# Revit family: Шкафы климатические навесные (без крыши)
name_source: partatom
category: Обобщенные модели
units: mm (PartAtom-declared; Revit-internal decimal feet)

## family parameters
Всегда вертикально = Да
Может служить основой для арматурных стержней = Нет
На основе рабочей плоскости = Нет
Общий = Нет
При загрузке вырезать с полостями = Нет
Размер круглого соединителя = Использовать диаметр
Тип детали = Нормальный
Точка расчета площади = Нет

## types (20) — shared parameters
ADSK_URL документации изделия = sert_shkt.PDF (ssd.ru)
ADSK_Единица измерения = шт
ADSK_Завод-изготовитель = АО СВЯЗЬСТРОЙДЕТАЛЬ
ADSK_Размер_Ширина = 678 мм
Материал Каркаса = RAL 7035
Материал букв = Металл красный
Материал ручек = Металл черный
Толщина -4 = -4 мм
Толщина 25 = 25 мм
Толщина 4 = 4 мм
Толщина 5 = 5 мм
zero-valued in all types: Ноль

## per-type parameters (varying)
| type | 3й-ряд | ADSK_URL страницы изделия | ADSK_Код изделия | ADSK_Масса_Текст | ADSK_Наименование | ADSK_Размер_Высота | ADSK_Размер_Глубина | Описание | Ручка центр | Ручки не центр |
| ШКТ-НВ-6U (700х350мм) | Нет | Шкаф климатический телекоммуникационный навесной 19. 6U(600x350)  ШКТ-НВ-6U-600-350 ССД ( 130411-00801 ) (ssd.ru) | 130411-00801 | 17 | Шкаф климатический телекоммуникационный навесной 19&quot. 6U(600x350)  ШКТ-НВ-6U-600-350 ССД | 290 мм | 350 мм | Шкаф климатический телекоммуникационный навесной 19&quot. 6U(600x350)  ШКТ-НВ-6U-600-350 ССД | Да | Нет |
| ШКТ-НВ-6U (700х450мм) | Нет | Шкаф климатический телекоммуникационный навесной 19.  6U(600x450)  ШКТ-НВ-6U-600-450 ССД ( 130411-00802 ) (ssd.ru) | 130411-00802 | 19 | Шкаф климатический телекоммуникационный навесной 19&quot.  6U(600x450)  ШКТ-НВ-6U-600-450 ССД | 290 мм | 450 мм | Шкаф климатический телекоммуникационный навесной 19&quot.  6U(600x450)  ШКТ-НВ-6U-600-450 ССД | Да | Нет |
| ШКТ-НВ-6U (700х550мм) | Нет | Шкаф климатический телекоммуникационный навесной 19.  6U(600x550)  ШКТ-НВ-6U-600-550 ССД ( 130411-00803 ) (ssd.ru) | 130411-00803 | 21 | Шкаф климатический телекоммуникационный навесной 19&quot.  6U(600x550)  ШКТ-НВ-6U-600-550 ССД | 290 мм | 550 мм | Шкаф климатический телекоммуникационный навесной 19&quot.  6U(600x450)  ШКТ-НВ-6U-600-450 ССД | Да | Нет |
| ШКТ-НВ-6U (700х650мм) | Нет | Шкаф климатический телекоммуникационный навесной 19. 6U(600x650)  ШКТ-НВ-6U-600-650 ССД ( 130411-00804 ) (ssd.ru) | 130411-00804 | 23 | Шкаф климатический телекоммуникационный навесной 19&quot. 6U(600x650)  ШКТ-НВ-6U-600-650 ССД | 290 мм | 650 мм | Шкаф климатический телекоммуникационный навесной 19&quot. 6U(600x650)  ШКТ-НВ-6U-600-650 ССД | Да | Нет |
| ШКТ-НВ-9U (700х350мм) | Нет | Шкаф климатический телекоммуникационный навесной 19.  9U(600x350)  ШКТ-НВ-9U-600-350 ССД ( 130411-00805 ) (ssd.ru) | 130411-00805 | 25 | Шкаф климатический телекоммуникационный навесной 19&quot.  9U(600x350)  ШКТ-НВ-9U-600-350 ССД | 440 мм | 350 мм | Шкаф климатический телекоммуникационный навесной 19&quot.  9U(600x350)  ШКТ-НВ-9U-600-350 ССД | Нет | Да |
| ШКТ-НВ-9U (700х450мм) | Нет | Шкаф климатический телекоммуникационный навесной 19. 9U(600x450)  ШКТ-НВ-9U-600-450 ССД ( 130411-00806 ) (ssd.ru) | 130411-00806 | 28 | Шкаф климатический телекоммуникационный навесной 19&quot. 9U(700x450)  ШКТ-НВ-9U-600-450 ССД | 440 мм | 450 мм | Шкаф климатический телекоммуникационный навесной 19&quot. 9U(700x450)  ШКТ-НВ-9U-600-450 ССД | Нет | Да |
| ШКТ-НВ-9U (700х550мм) | Нет | Шкаф климатический телекоммуникационный навесной 19.  9U(600x550)  ШКТ-НВ-9U-600-550 ССД ( 130411-00807 ) (ssd.ru) | 130411-00807 | 31 | Шкаф климатический телекоммуникационный навесной 19&quot.  9U(600x550)  ШКТ-НВ-9U-600-550 ССД | 440 мм | 550 мм | Шкаф климатический телекоммуникационный навесной 19&quot.  9U(600x550)  ШКТ-НВ-9U-600-550 ССД | Нет | Да |
| ШКТ-НВ-9U (700х650мм) | Нет | Шкаф климатический телекоммуникационный навесной 19. 9U(600x650)  ШКТ-НВ-9U-600-650 ССД ( 130411-00808 ) (ssd.ru) | 130411-00808 | 34 | Шкаф климатический телекоммуникационный навесной 19&quot. 9U(600x650)  ШКТ-НВ-9U-600-650 ССД | 440 мм | 650 мм | Шкаф климатический телекоммуникационный навесной 19&quot. 9U(600x650)  ШКТ-НВ-9U-600-650 ССД | Нет | Да |
| ШКТ-НВ-12U (600х350мм) | Нет | Шкаф климатический телекоммуникационный навесной 19. 12U(600x350)  ШКТ-НВ-12U-600-350 ССД ( 130411-00809 ) (ssd.ru) | 130411-00809 | 36 | Шкаф климатический телекоммуникационный навесной 19&quot. 12U(600x350)  ШКТ-НВ-12U-600-350 ССД | 580 мм | 350 мм | Шкаф климатический телекоммуникационный навесной 19&quot. 12U(600x350)  ШКТ-НВ-12U-600-350 ССД | Нет | Да |
| ШКТ-НВ-12U (600х450мм) | Нет | Шкаф климатический телекоммуникационный навесной 19. 12U(600x450)  ШКТ-НВ-12U-600-450 ССД ( 130411-00810 ) (ssd.ru) | 130411-00810 | 40 | Шкаф климатический телекоммуникационный навесной 19&quot. 12U(600x450)  ШКТ-НВ-12U-600-450 ССД | 580 мм | 450 мм | Шкаф климатический телекоммуникационный навесной 19&quot. 12U(600x450)  ШКТ-НВ-12U-600-450 ССД | Нет | Да |
| ШКТ-НВ-12U (600х550мм) | Нет | Шкаф телекоммуникационный климатический навесной 19. 12U(600x550)  ШКТ-НВ-12U-600-550 ССД ( 130411-00811 ) (ssd.ru) | 130411-00811 | 43 | Шкаф телекоммуникационный климатический навесной 19&quot. 12U(600x550)  ШКТ-НВ-12U-600-550 ССД | 580 мм | 550 мм | Шкаф телекоммуникационный климатический навесной 19&quot. 12U(600x550)  ШКТ-НВ-12U-600-550 ССД | Нет | Да |
| ШКТ-НВ-12U (600х650мм) | Нет | Шкаф климатический телекоммуникационный навесной 19. 12U(600x650)  ШКТ-НВ-12U-600-650 ССД ( 130411-00812 ) (ssd.ru) | 130411-00812 | 47 | Шкаф климатический телекоммуникационный навесной 19&quot. 12U(600x650)  ШКТ-НВ-12U-600-650 ССД | 580 мм | 650 мм | Шкаф климатический телекоммуникационный навесной 19&quot. 12U(600x650)  ШКТ-НВ-12U-600-650 ССД | Нет | Да |
| ШКТ-НВ-15U (600х350мм) | Да | Шкаф климатический телекоммуникационный навесной 19. 15U(600x350)  ШКТ-НВ-15U-600-350 ССД ( 130411-00813 ) (ssd.ru) | 130411-00813 | 42 | Шкаф климатический телекоммуникационный навесной 19&quot. 15U(600x350)  ШКТ-НВ-15U-600-350 ССД | 714 мм | 350 мм | Шкаф климатический телекоммуникационный навесной 19&quot. 15U(600x350)  ШКТ-НВ-15U-600-350 ССД | Нет | Да |
| ШКТ-НВ-15U (600х450мм) | Да | Шкаф климатический телекоммуникационный навесной 19. 15U(600x450)  ШКТ-НВ-15U-600-450 ССД ( 130411-00814 ) (ssd.ru) | 130411-00814 | 46 | Шкаф климатический телекоммуникационный навесной 19&quot. 15U(600x450)  ШКТ-НВ-15U-600-450 ССД | 714 мм | 450 мм | Шкаф климатический телекоммуникационный навесной 19&quot. 15U(600x450)  ШКТ-НВ-15U-600-450 ССД | Нет | Да |
| ШКТ-НВ-15U (600х550мм) | Да | Шкаф климатический телекоммуникационный навесной 19. 15U(600x550)  ШКТ-НВ-15U-600-550 ССД ( 130411-00815 ) (ssd.ru) | 130411-00815 | 50 | Шкаф климатический телекоммуникационный навесной 19&quot. 15U(600x550)  ШКТ-НВ-15U-600-550 ССД | 714 мм | 550 мм | Шкаф климатический телекоммуникационный навесной 19&quot. 15U(600x550)  ШКТ-НВ-15U-600-550 ССД | Нет | Да |
| ШКТ-НВ-15U (600х650мм) | Да | Шкаф климатический телекоммуникационный навесной 19. 15U(600x650)  ШКТ-НВ-15U-600-650 ССД ( 130411-00816 ) (ssd.ru) | 130411-00816 | 54 | Шкаф климатический телекоммуникационный навесной 19&quot. 15U(600x650)  ШКТ-НВ-15U-600-650 ССД | 714 мм | 650 мм | Шкаф климатический телекоммуникационный навесной 19&quot. 15U(600x650)  ШКТ-НВ-15U-600-650 ССД | Нет | Да |
| ШКТ-НВ-18U (700х350мм) | Да | Шкаф климатический телекоммуникационный навесной 19. 18U(600x350)  ШКТ-НВ-18U-600-350 ССД ( 130411-00817 ) (ssd.ru) | 130411-00817 | 48 | Шкаф климатический телекоммуникационный навесной 19&quot. 18U(600x350)  ШКТ-НВ-18U-600-350 ССД | 847 мм | 350 мм | Шкаф климатический телекоммуникационный навесной 19&quot. 18U(600x350)  ШКТ-НВ-18U-600-350 ССД | Нет | Да |
| ШКТ-НВ-18U (700х450мм) | Да | Шкаф климатический телекоммуникационный навесной 19. 18U(600x450)  ШКТ-НВ-18U-600-450 ССД ( 130411-00818 ) (ssd.ru) | 130411-00818 | 52 | Шкаф климатический телекоммуникационный навесной 19&quot. 18U(600x450)  ШКТ-НВ-18U-600-450 ССД | 847 мм | 450 мм | Шкаф климатический телекоммуникационный навесной 19&quot. 18U(600x450)  ШКТ-НВ-18U-600-450 ССД | Нет | Да |
| ШКТ-НВ-18U (700х550мм) | Да | Шкаф климатический телекоммуникационный навесной 19. 18U(600x550)  ШКТ-НВ-18U-600-550 ССД ( 130411-00819 ) (ssd.ru) | 130411-00819 | 57 | Шкаф климатический телекоммуникационный навесной 19&quot. 18U(600x550)  ШКТ-НВ-18U-600-550 ССД | 847 мм | 550 мм | Шкаф климатический телекоммуникационный навесной 19&quot. 18U(600x550)  ШКТ-НВ-18U-600-550 ССД | Нет | Да |
| ШКТ-НВ-18U (700х650мм) | Да | Шкаф климатический телекоммуникационный навесной 19. 18U(600x650)  ШКТ-НВ-18U-600-650 ССД ( 130411-00820 ) (ssd.ru) | 130411-00820 | 61 | Шкаф климатический телекоммуникационный навесной 19&quot. 18U(600x650)  ШКТ-НВ-18U-600-650 ССД | 847 мм | 650 мм | Шкаф климатический телекоммуникационный навесной 19&quot. 18U(600x650)  ШКТ-НВ-18U-600-650 ССД | Нет | Да |

note: column(s) folded — value = type name in every type: ADSK_Наименование краткое

## geometry (parser evidence)
native form markers: Blend x4
no freeform markers — native parametric forms only
